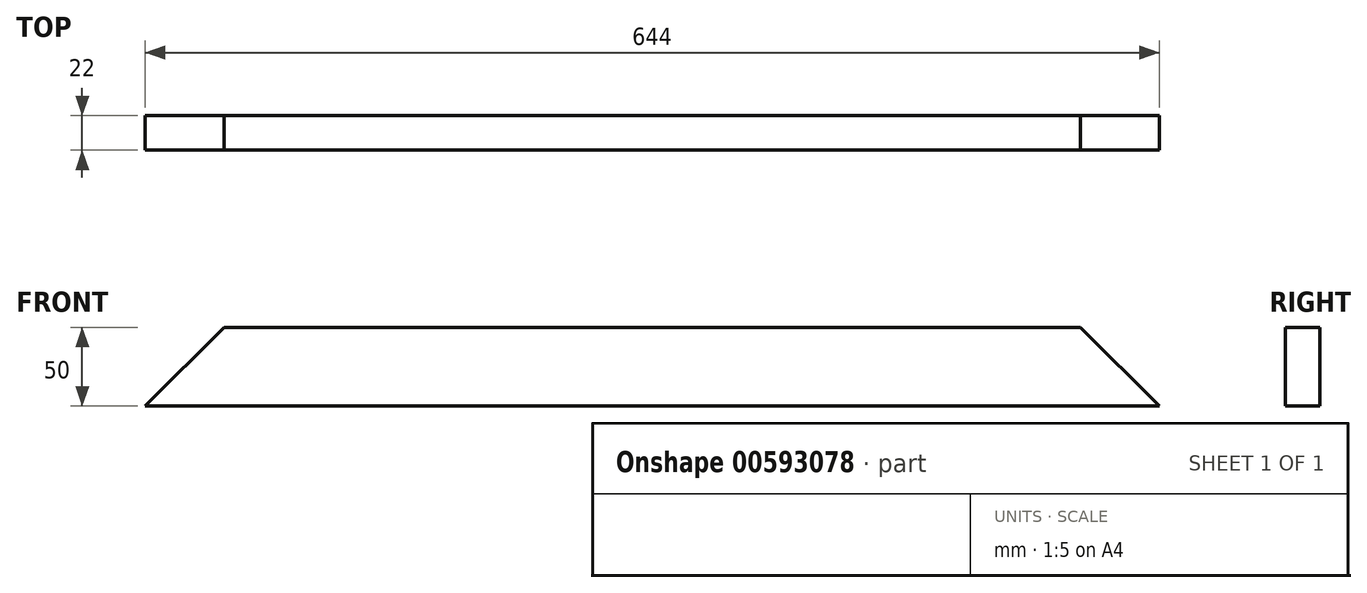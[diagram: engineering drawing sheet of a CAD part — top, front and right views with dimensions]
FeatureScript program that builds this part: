
annotation { "Feature Type Name" : "Feature", "Feature Type Description" : "" }
export const myFeature = defineFeature(function(context is Context, id is Id, definition is map)
    precondition{}
    {
        {
            var Q0;
            Q0=qCreatedBy(makeId("Front.planeOp"),FACE);
            var sketch = newSketch(context, id + "F0", { "sketchPlane" : qUnion([Q0])});
            skLineSegment(sketch, "E0.bottom", {"start": v(-272, 0) * mm, "end": v(272, 0) * mm});
            skLineSegment(sketch, "E0.top", {"start": v(-322, -50) * mm, "end": v(322, -50) * mm});
            skLineSegment(sketch, "E1", {"start": v(-322, -50) * mm, "end": v(-272, 0) * mm});
            skLineSegment(sketch, "E2", {"start": v(322, -50) * mm, "end": v(272, 0) * mm});
            skSolve(sketch);
        }
        {
            var Q0;
            Q0=qSketchRegion(id+"F0",true);
            extrude(context, id + "F1", {"entities" : qUnion([Q0]), "depth" : 22 * mm, "offsetDistance" : 25 * mm});
        }
    });
